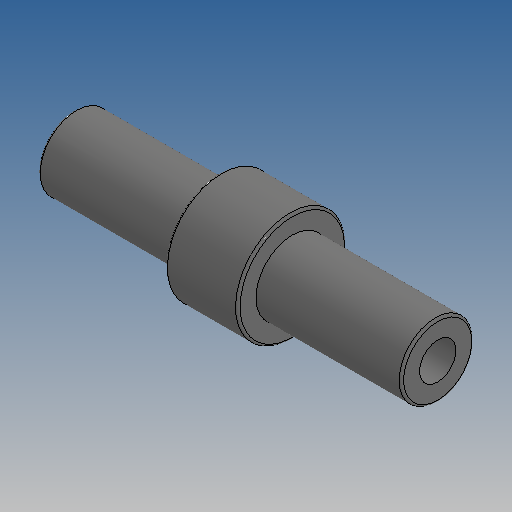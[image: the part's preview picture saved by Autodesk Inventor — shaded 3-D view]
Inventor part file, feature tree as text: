
AUTODESK INVENTOR PART (.ipt)
format: ipt  version: 2025 (Build 290162010, 162A)  size: 158,208 bytes
history: native  units: mm
features: revolve x1, fillet x1, sketch x1
ambient origin geometry x8: Origin, YZ Plane, XZ Plane, XY Plane, X Axis, Y Axis, Z Axis, Center Point
bodies: Solid1 (feature_tree)
feature tree (3):
  revolve  "Revolution1"  [1 undecoded]
  fillet  "Fillet1"  Radius=3.2mm
  sketch  "Sketch1"  dims[d0=8.0mm d2=4.8mm d3=3.2mm d4=1.6mm d5=4.0mm d6=3.2mm d7=90.0deg d8=0.1mm]
note: 1 required parameter value undecoded (feature->parameter linkage not recoverable at this tier; creation-order binding heuristic only, values carry confidence <= 0.55)
